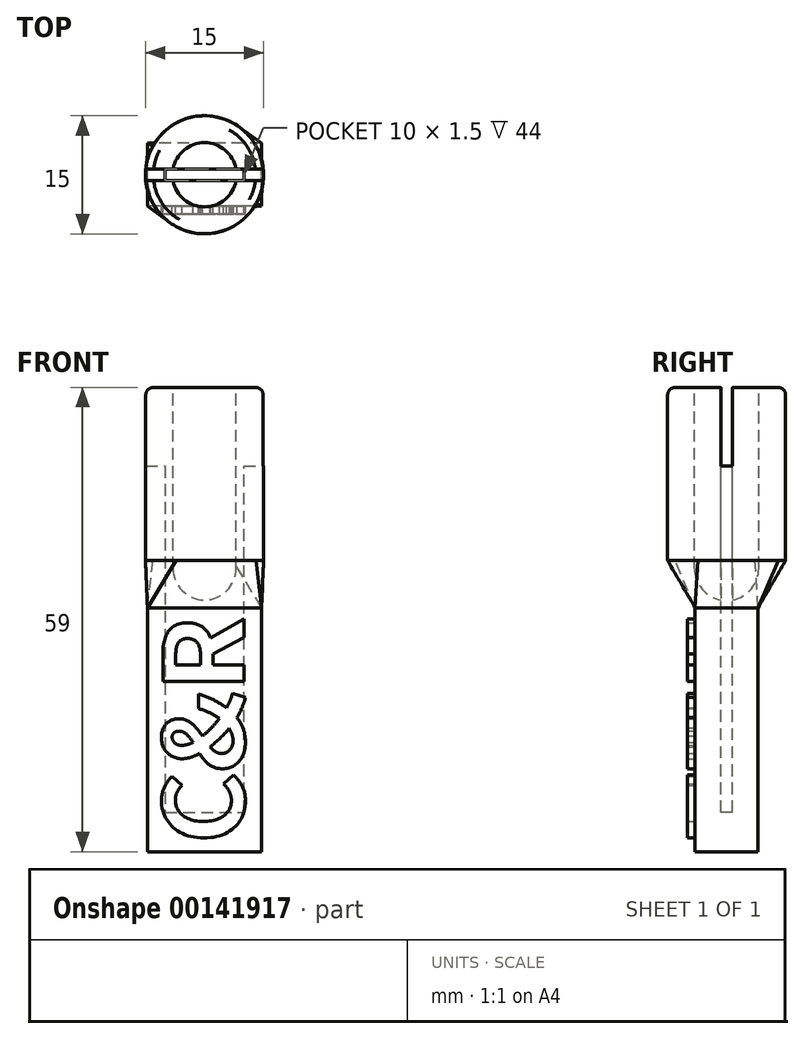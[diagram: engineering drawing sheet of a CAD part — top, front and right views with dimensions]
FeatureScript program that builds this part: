
annotation { "Feature Type Name" : "Feature", "Feature Type Description" : "" }
export const myFeature = defineFeature(function(context is Context, id is Id, definition is map)
    precondition{}
    {
        {
            var Q0;
            Q0=qCreatedBy(makeId("Top.planeOp"),FACE);
            var sketch = newSketch(context, id + "F0", { "sketchPlane" : qUnion([Q0])});
            skLineSegment(sketch, "E0.bottom", {"start": v(7.25, -4) * mm, "end": v(-7.25, -4) * mm});
            skLineSegment(sketch, "E0.top", {"start": v(7.25, 4) * mm, "end": v(-7.25, 4) * mm});
            skLineSegment(sketch, "E0.left", {"start": v(7.25, -4) * mm, "end": v(7.25, 4) * mm});
            skLineSegment(sketch, "E0.right", {"start": v(-7.25, -4) * mm, "end": v(-7.25, 4) * mm});
            skPoint(sketch, "E0.middle", {"position": v(0, 0) * mm});
            skSolve(sketch);
        }
        {
            var Q0;
            Q0 = qSketchRegion(id + "F0", true);
            extrude(context, id + "F1", {"entities" : qUnion([Q0]), "depth" : 31 * mm});
        }
        {
            var Q0;
            Q0=makeQuery(id+"F1.opExtrude","CAP_FACE",FACE,{"disambiguationData":[OSD([sQuery(id+"F0.wireOp",EDGE,"E0.bottom"),sQuery(id+"F0.wireOp",EDGE,"E0.top"),sQuery(id+"F0.wireOp",EDGE,"E0.left"),sQuery(id+"F0.wireOp",EDGE,"E0.right")])],"isStart":false});
            cPlane(context, id + "F2", {"entities" : qUnion([Q0]), "cplaneType" : CPlaneType.OFFSET, "offset" : 6 * mm, "width" : 150 * mm, "height" : 150 * mm});
        }
        {
            var Q0;
            Q0=qCreatedBy(id+"F2.planeOp",FACE);
            var sketch = newSketch(context, id + "F3", { "sketchPlane" : qUnion([Q0])});
            skCircle(sketch, "E1", {"center": v(0, 0) * mm, "radius": 7.5 * mm});
            skSolve(sketch);
        }
        {
            var Q1;
            Q1=makeQuery(id+"F1.opExtrude","CAP_FACE",FACE,{"disambiguationData":[OSD([sQuery(id+"F0.wireOp",EDGE,"E0.bottom"),sQuery(id+"F0.wireOp",EDGE,"E0.top"),sQuery(id+"F0.wireOp",EDGE,"E0.left"),sQuery(id+"F0.wireOp",EDGE,"E0.right")])],"isStart":false});
            var Q2;
            Q2=makeQuery(id+"F3.imprint","IMPRINT",FACE,{"disambiguationData":[TD([[makeQuery(id+"F3.imprint","IMPRINT",EDGE,{"derivedFrom":sQuery(id+"F3.wireOp",EDGE,"E1")}),1.0]])]});
            loft(context, id + "F4", {"operationType" : NewBodyOperationType.ADD, "sheetProfilesArray" : [{ "sheetProfileEntities" : qUnion([Q1]) }, { "sheetProfileEntities" : qUnion([Q2]) }]});
        }
        {
            var Q0;
            Q0=makeQuery(id+"F4.opLoft","CAP_FACE",FACE,{"disambiguationData":[OSD([makeQuery(id+"F3.imprint","IMPRINT",FACE,{"disambiguationData":[TD([[makeQuery(id+"F3.imprint","IMPRINT",EDGE,{"derivedFrom":sQuery(id+"F3.wireOp",EDGE,"E1")}),1.0]])]})])],"isStart":true});
            extrude(context, id + "F5", {"entities" : qUnion([Q0]), "operationType" : NewBodyOperationType.ADD, "depth" : 22 * mm});
        }
        {
            var Q0;
            Q0=makeQuery(id+"F5.opExtrude","CAP_FACE",FACE,{"disambiguationData":[OSD([makeQuery(id+"F3.imprint","IMPRINT",FACE,{"disambiguationData":[TD([[makeQuery(id+"F3.imprint","IMPRINT",EDGE,{"derivedFrom":sQuery(id+"F3.wireOp",EDGE,"E1")}),1.0]])]})])],"isStart":false});
            var sketch = newSketch(context, id + "F6", { "sketchPlane" : qUnion([Q0])});
            skCircle(sketch, "E2", {"center": v(0, 0) * mm, "radius": 4.08 * mm});
            skSolve(sketch);
        }
        {
            var Q0;
            Q0 = qSketchRegion(id + "F6", true);
            extrude(context, id + "F7", {"entities" : qUnion([Q0]), "operationType" : NewBodyOperationType.REMOVE, "oppositeDirection" : true, "depth" : 23 * mm});
        }
        {
            var Q0;
            Q0=makeQuery(id+"F7.boolean.opBoolean","COPY",FACE,{"derivedFrom":makeQuery(id+"F7.opExtrude","CAP_FACE",FACE,{"disambiguationData":[OSD([sQuery(id+"F6.wireOp",EDGE,"E2")])],"isStart":false})});
            var sketch = newSketch(context, id + "F8", { "sketchPlane" : qUnion([Q0])});
            skPoint(sketch, "E3", {"position": v(4.08, 0) * mm});
            skPoint(sketch, "E4", {"position": v(-4.08, 0) * mm});
            skSolve(sketch);
        }
        {
            var Q0;
            Q0=qCreatedBy(makeId("Front.planeOp"),FACE);
            var sketch = newSketch(context, id + "F9", { "sketchPlane" : qUnion([Q0])});
            skPoint(sketch, "E5", {"position": v(-4.08, 36) * mm});
            skPoint(sketch, "E6", {"position": v(4.08, 36) * mm});
            skLineSegment(sketch, "E7", {"start": v(-4.08, 41.74) * mm, "end": v(-4.07, 28.58) * mm, "construction": true});
            skLineSegment(sketch, "E8", {"start": v(4.07, 41.74) * mm, "end": v(4.08, 28.58) * mm, "construction": true});
            skPoint(sketch, "E9", {"position": v(0, 36) * mm});
            skPoint(sketch, "E10", {"position": v(0, 31.92) * mm});
            skArc(sketch, "E11", {"start": v(-4.08, 36) * mm, "mid": v(-2.88, 33.12) * mm, "end": v(0, 31.92) * mm});
            skLineSegment(sketch, "E12", {"start": v(-4.08, 36) * mm, "end": v(0, 36) * mm});
            skLineSegment(sketch, "E13", {"start": v(0, 31.92) * mm, "end": v(0, 36) * mm});
            skLineSegment(sketch, "E14", {"start": v(0, 36) * mm, "end": v(-4.08, 36) * mm});
            skLineSegment(sketch, "E15", {"start": v(0, 36.49) * mm, "end": v(0, 29.23) * mm, "construction": true});
            skPoint(sketch, "E15.endSnap0", {"position": v(0, 33.96) * mm});
            skSolve(sketch);
        }
        {
            var Q0;
            Q0 = qSketchRegion(id + "F9", true);
            var Q1;
            Q1=sQuery(id+"F9.wireOp",EDGE,"E15");
            revolve(context, id + "F10", {"operationType" : NewBodyOperationType.REMOVE, "entities" : qUnion([Q0]), "axis" : qUnion([Q1]), "revolveType" : RevolveType.FULL, "oppositeDirection" : true});
        }
        {
            var Q0;
            Q0=qCreatedBy(makeId("Front.planeOp"),FACE);
            var sketch = newSketch(context, id + "F11", { "sketchPlane" : qUnion([Q0])});
            skLineSegment(sketch, "E16", {"start": v(0, -7.24) * mm, "end": v(0, 62) * mm, "construction": true});
            skLineSegment(sketch, "E17", {"start": v(0, 36) * mm, "end": v(-5, 36) * mm});
            skLineSegment(sketch, "E18", {"start": v(0, 36) * mm, "end": v(5, 36) * mm});
            skLineSegment(sketch, "E19", {"start": v(-5, 36) * mm, "end": v(-5, 5) * mm});
            skLineSegment(sketch, "E20", {"start": v(5, 5) * mm, "end": v(5, 36) * mm});
            skLineSegment(sketch, "E21", {"start": v(-5, 5) * mm, "end": v(5, 5) * mm});
            skLineSegment(sketch, "E22", {"start": v(-5, 36) * mm, "end": v(-5, 59.53) * mm});
            skLineSegment(sketch, "E23", {"start": v(-5, 59.53) * mm, "end": v(5, 59.53) * mm});
            skLineSegment(sketch, "E24", {"start": v(5, 59.53) * mm, "end": v(5, 36) * mm});
            skSolve(sketch);
        }
        {
            var Q0;
            Q0 = qSketchRegion(id + "F11", true);
            extrude(context, id + "F12", {"entities" : qUnion([Q0]), "operationType" : NewBodyOperationType.REMOVE, "oppositeDirection" : true, "depth" : .75 * mm, "hasSecondDirection" : true, "secondDirectionOppositeDirection" : false, "secondDirectionDepth" : .75 * mm});
        }
        {
            var Q0;
            Q0=makeQuery(id+"F5.opExtrude","CAP_EDGE",EDGE,{"disambiguationData":[OSD([sQuery(id+"F0.wireOp",EDGE,"E0.bottom"),sQuery(id+"F0.wireOp",EDGE,"E0.top"),sQuery(id+"F0.wireOp",EDGE,"E0.left"),sQuery(id+"F0.wireOp",EDGE,"E0.right"),sQuery(id+"F3.wireOp",EDGE,"E1")])],"isStart":false});
            fillet(context, id + "F13", {"entities" : qUnion([Q0]), "radius" : 1 * mm, "tangentPropagation" : true, "allowEdgeOverflow" : false});
        }
        {
            var Q0;
            Q0=makeQuery(id+"F1.opExtrude","SWEPT_FACE",FACE,{"disambiguationData":[OSD([sQuery(id+"F0.wireOp",EDGE,"E0.bottom")])]});
            var sketch = newSketch(context, id + "F14", { "sketchPlane" : qUnion([Q0])});
            skText(sketch, "E25", { "text": "C&R", "fontName": "NotoSansCJKsc-Bold.otf"});
            skLineSegment(sketch, "E26", {"start": v(0, -18.22) * mm, "end": v(0, 53.8) * mm, "construction": true});
            skPoint(sketch, "E26.startSnap0", {"position": v(0, 0) * mm});
            skPoint(sketch, "E26.endSnap0", {"position": v(0, 31) * mm});
            skPoint(sketch, "E27", {"position": v(0, 1) * mm});
            const initialGuessF14  = {"E25": [0.005, 0.001, 0, 1, 0.01]};
            skSetInitialGuess(sketch, initialGuessF14);
            skSolve(sketch);
        }
        {
            var Q0;
            Q0 = qSketchRegion(id + "F14", true);
            extrude(context, id + "F15", {"entities" : qUnion([Q0]), "operationType" : NewBodyOperationType.ADD, "depth" : 1 * mm});
        }
        {
            var Q0;
            Q0=makeQuery(id+"F5.opExtrude","CAP_FACE",FACE,{"disambiguationData":[OSD([makeQuery(id+"F3.imprint","IMPRINT",FACE,{"disambiguationData":[TD([[makeQuery(id+"F3.imprint","IMPRINT",EDGE,{"derivedFrom":sQuery(id+"F3.wireOp",EDGE,"E1")}),1.0]])]})])],"isStart":false});
            var sketch = newSketch(context, id + "F16", { "sketchPlane" : qUnion([Q0])});
            skLineSegment(sketch, "E28.bottom", {"start": v(-8.3, 0.75) * mm, "end": v(8.3, 0.75) * mm});
            skLineSegment(sketch, "E28.top", {"start": v(-8.3, -0.75) * mm, "end": v(8.3, -0.75) * mm});
            skLineSegment(sketch, "E28.left", {"start": v(-8.3, 0.75) * mm, "end": v(-8.3, -0.75) * mm});
            skLineSegment(sketch, "E28.right", {"start": v(8.3, 0.75) * mm, "end": v(8.3, -0.75) * mm});
            skPoint(sketch, "E29", {"position": v(0, 0) * mm});
            skPoint(sketch, "E29.positionSnap0", {"position": v(0, 0.75) * mm});
            skPoint(sketch, "E29.positionSnap1", {"position": v(8.3, 0) * mm});
            skSolve(sketch);
        }
        {
            var Q0;
            Q0 = qSketchRegion(id + "F16", true);
            extrude(context, id + "F17", {"entities" : qUnion([Q0]), "operationType" : NewBodyOperationType.REMOVE, "oppositeDirection" : true, "depth" : 10 * mm});
        }
    });
